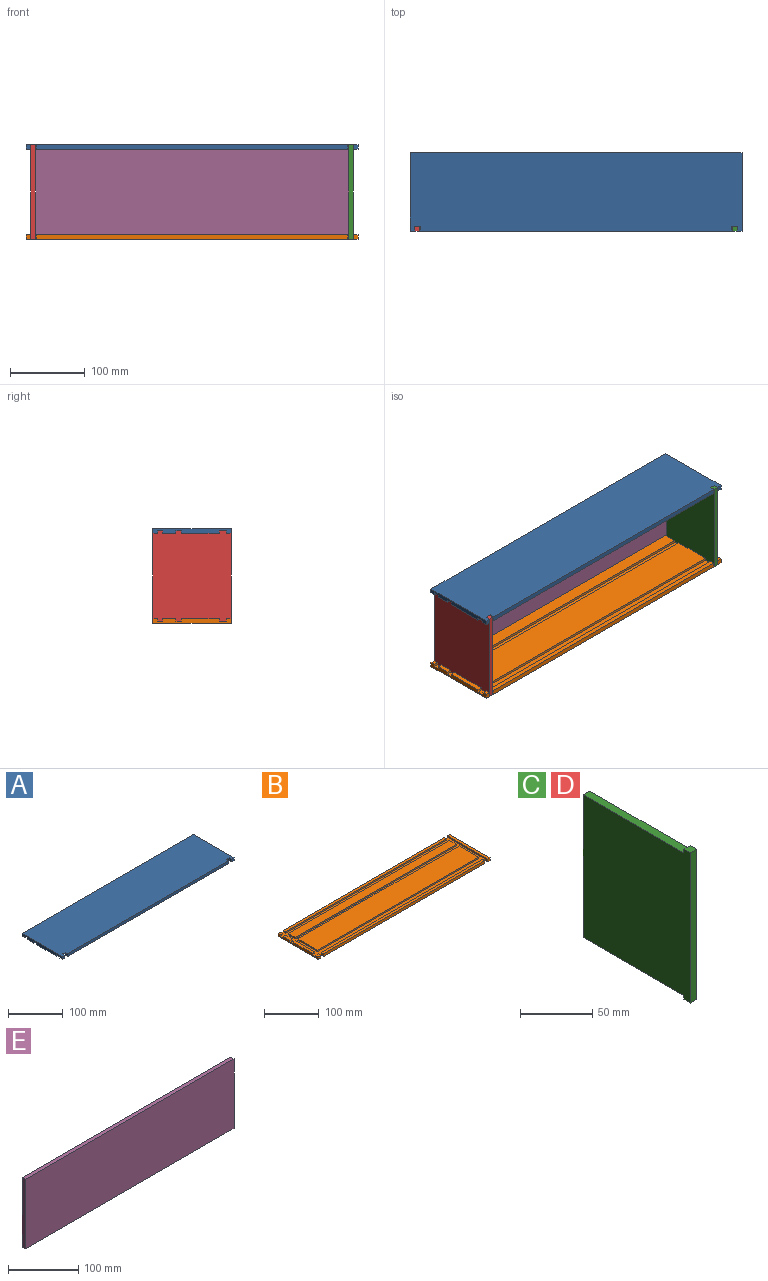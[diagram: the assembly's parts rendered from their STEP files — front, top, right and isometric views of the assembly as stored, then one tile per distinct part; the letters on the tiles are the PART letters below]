
ASSEMBLY  parts=5 mates=4
PART A: 44 faces, bbox 444.5x104.8x6.4 mm
  f0: plane 417.51x6.35mm, normal (0,0,-1), area 2651.2mm2, adj f12,f13,f14,f20
  f1: plane 6.35x6.35mm, normal (0,0,-1), area 40.3mm2, adj f8,f9,f10,f27
  f2: plane 50.8x6.35mm, normal (0,0,-1), area 322.6mm2, adj f8,f36,f37,f38
  f3: plane 17.46x6.35mm, normal (0,0,-1), area 110.9mm2, adj f8,f33,f34,f35
  f4: plane 417.51x6.35mm, normal (0,0,-1), area 2651.2mm2, adj f7,f28,f29,f30
  f5: plane 104.78x6.35mm, normal (0,0,-1), area 665.3mm2, adj f6,f7,f16,f17
  f6: plane 104.78x6.35mm, normal (1,0,0), area 665.3mm2, adj f5,f7,f17,f18
  f7: plane 444.5x6.35mm, normal (0,1,0), area 2777.2mm2, adj f4,f5,f6,f8,f16,f18,f19,f28
  f8: plane 104.78x6.35mm, normal (-1,0,0), area 589.7mm2, adj f1,f2,f3,f7,f9,f18,f19,f27
  f9: plane 6.35x6.35mm, normal (0,-1,0), area 40.3mm2, adj f1,f8,f10,f18
  f10: plane 6.35x6.35mm, normal (1,0,0), area 40.3mm2, adj f1,f9,f11,f18,f27
  f11: plane 7.14x3.18mm, normal (0,-1,0), area 22.7mm2, adj f10,f12,f18,f41
  f12: plane 6.35x6.35mm, normal (-1,0,0), area 40.3mm2, adj f0,f11,f13,f18,f20
  f13: plane 417.51x6.35mm, normal (0,-1,0), area 2651.2mm2, adj f0,f12,f14,f18
  f14: plane 6.35x6.35mm, normal (1,0,0), area 40.3mm2, adj f0,f13,f15,f18,f20
  f15: plane 7.14x3.18mm, normal (0,-1,0), area 22.7mm2, adj f14,f16,f18,f41
  f16: plane 104.78x6.35mm, normal (-1,0,0), area 352.8mm2, adj f5,f7,f15,f17,f18,f41
  f17: plane 6.35x6.35mm, normal (0,-1,0), area 40.3mm2, adj f5,f6,f16,f18
  f18: plane 444.5x104.78mm, normal (0,0,1), area 46481.8mm2, adj f6,f7,f8,f9,f10,f11,f12,f13
  f19: plane 6.35x6.35mm, normal (0,0,-1), area 40.3mm2, adj f7,f8,f31,f32
  f20: plane 417.51x3.18mm, normal (0,1,0), area 1325.6mm2, adj f0,f12,f14,f41
  f21: plane 417.51x3.18mm, normal (0,-1,0), area 1325.6mm2, adj f22,f40,f41,f43
  f22: plane 17.46x3.18mm, normal (-1,0,0), area 55.4mm2, adj f21,f23,f41,f43
  f23: plane 417.51x3.18mm, normal (0,1,0), area 1325.6mm2, adj f22,f40,f41,f43
  f24: plane 417.51x3.18mm, normal (0,-1,0), area 1325.6mm2, adj f25,f39,f41,f42
  f25: plane 50.8x3.18mm, normal (-1,0,0), area 161.3mm2, adj f24,f26,f41,f42
  f26: plane 417.51x3.18mm, normal (0,1,0), area 1325.6mm2, adj f25,f39,f41,f42
  f27: plane 6.35x3.18mm, normal (0,1,0), area 20.2mm2, adj f1,f8,f10,f41
  f28: plane 6.35x3.18mm, normal (1,0,0), area 20.2mm2, adj f4,f7,f29,f41
  f29: plane 417.51x3.18mm, normal (0,-1,0), area 1325.6mm2, adj f4,f28,f30,f41
  f30: plane 6.35x3.18mm, normal (-1,0,0), area 20.2mm2, adj f4,f7,f29,f41
  f31: plane 6.35x3.18mm, normal (1,0,0), area 20.2mm2, adj f7,f19,f32,f41
  f32: plane 6.35x3.18mm, normal (0,-1,0), area 20.2mm2, adj f8,f19,f31,f41
  f33: plane 6.35x3.18mm, normal (0,1,0), area 20.2mm2, adj f3,f8,f34,f41
  f34: plane 17.46x3.18mm, normal (1,0,0), area 55.4mm2, adj f3,f33,f35,f41
  f35: plane 6.35x3.18mm, normal (0,-1,0), area 20.2mm2, adj f3,f8,f34,f41
  f36: plane 6.35x3.18mm, normal (0,1,0), area 20.2mm2, adj f2,f8,f37,f41
  f37: plane 50.8x3.18mm, normal (1,0,0), area 161.3mm2, adj f2,f36,f38,f41
  f38: plane 6.35x3.18mm, normal (0,-1,0), area 20.2mm2, adj f2,f8,f37,f41
  f39: plane 50.8x3.18mm, normal (1,0,0), area 161.3mm2, adj f24,f26,f41,f42
  f40: plane 17.46x3.18mm, normal (1,0,0), area 55.4mm2, adj f21,f23,f41,f43
  f41: plane 438.15x98.43mm, normal (0,0,-1), area 11499.5mm2, adj f7,f8,f11,f15,f16,f20,f21,f22
  f42: plane 417.51x50.8mm, normal (0,0,-1), area 21209.6mm2, adj f24,f25,f26,f39
  f43: plane 417.51x17.46mm, normal (0,0,-1), area 7290.8mm2, adj f21,f22,f23,f40
PART B: 44 faces, bbox 444.5x104.8x6.4 mm
  f0: plane 444.5x6.35mm, normal (0,1,0), area 2777.2mm2, adj f1,f4,f5,f8,f9,f17,f19,f28
  f1: plane 104.78x6.35mm, normal (-1,0,0), area 589.7mm2, adj f0,f3,f6,f7,f8,f10,f19,f27
  f2: plane 417.51x6.35mm, normal (0,0,1), area 2651.2mm2, adj f13,f14,f15,f20
  f3: plane 6.35x6.35mm, normal (0,0,1), area 40.3mm2, adj f1,f10,f11,f27
  f4: plane 104.78x6.35mm, normal (0,0,1), area 665.3mm2, adj f0,f9,f17,f18
  f5: plane 417.51x6.35mm, normal (0,0,1), area 2651.2mm2, adj f0,f28,f29,f30
  f6: plane 17.46x6.35mm, normal (0,0,1), area 110.9mm2, adj f1,f33,f34,f35
  f7: plane 50.8x6.35mm, normal (0,0,1), area 322.6mm2, adj f1,f36,f37,f38
  f8: plane 6.35x6.35mm, normal (0,0,1), area 40.3mm2, adj f0,f1,f31,f32
  f9: plane 104.78x6.35mm, normal (1,0,0), area 665.3mm2, adj f0,f4,f18,f19
  f10: plane 6.35x6.35mm, normal (0,-1,0), area 40.3mm2, adj f1,f3,f11,f19
  f11: plane 6.35x6.35mm, normal (1,0,0), area 40.3mm2, adj f3,f10,f12,f19,f27
  f12: plane 7.14x3.18mm, normal (0,-1,0), area 22.7mm2, adj f11,f13,f19,f41
  f13: plane 6.35x6.35mm, normal (-1,0,0), area 40.3mm2, adj f2,f12,f14,f19,f20
  f14: plane 417.51x6.35mm, normal (0,-1,0), area 2651.2mm2, adj f2,f13,f15,f19
  f15: plane 6.35x6.35mm, normal (1,0,0), area 40.3mm2, adj f2,f14,f16,f19,f20
  f16: plane 7.14x3.18mm, normal (0,-1,0), area 22.7mm2, adj f15,f17,f19,f41
  f17: plane 104.78x6.35mm, normal (-1,0,0), area 352.8mm2, adj f0,f4,f16,f18,f19,f41
  f18: plane 6.35x6.35mm, normal (0,-1,0), area 40.3mm2, adj f4,f9,f17,f19
  f19: plane 444.5x104.78mm, normal (0,0,-1), area 46481.8mm2, adj f0,f1,f9,f10,f11,f12,f13,f14
  f20: plane 417.51x3.18mm, normal (0,1,0), area 1325.6mm2, adj f2,f13,f15,f41
  f21: plane 417.51x3.18mm, normal (0,-1,0), area 1325.6mm2, adj f22,f40,f41,f43
  f22: plane 17.46x3.18mm, normal (-1,0,0), area 55.4mm2, adj f21,f23,f41,f43
  f23: plane 417.51x3.18mm, normal (0,1,0), area 1325.6mm2, adj f22,f40,f41,f43
  f24: plane 417.51x3.18mm, normal (0,-1,0), area 1325.6mm2, adj f25,f39,f41,f42
  f25: plane 50.8x3.18mm, normal (-1,0,0), area 161.3mm2, adj f24,f26,f41,f42
  f26: plane 417.51x3.18mm, normal (0,1,0), area 1325.6mm2, adj f25,f39,f41,f42
  f27: plane 6.35x3.18mm, normal (0,1,0), area 20.2mm2, adj f1,f3,f11,f41
  f28: plane 6.35x3.18mm, normal (1,0,0), area 20.2mm2, adj f0,f5,f29,f41
  f29: plane 417.51x3.18mm, normal (0,-1,0), area 1325.6mm2, adj f5,f28,f30,f41
  f30: plane 6.35x3.18mm, normal (-1,0,0), area 20.2mm2, adj f0,f5,f29,f41
  f31: plane 6.35x3.18mm, normal (1,0,0), area 20.2mm2, adj f0,f8,f32,f41
  f32: plane 6.35x3.18mm, normal (0,-1,0), area 20.2mm2, adj f1,f8,f31,f41
  f33: plane 6.35x3.18mm, normal (0,1,0), area 20.2mm2, adj f1,f6,f34,f41
  f34: plane 17.46x3.18mm, normal (1,0,0), area 55.4mm2, adj f6,f33,f35,f41
  f35: plane 6.35x3.18mm, normal (0,-1,0), area 20.2mm2, adj f1,f6,f34,f41
  f36: plane 6.35x3.18mm, normal (0,1,0), area 20.2mm2, adj f1,f7,f37,f41
  f37: plane 50.8x3.18mm, normal (1,0,0), area 161.3mm2, adj f7,f36,f38,f41
  f38: plane 6.35x3.18mm, normal (0,-1,0), area 20.2mm2, adj f1,f7,f37,f41
  f39: plane 50.8x3.18mm, normal (1,0,0), area 161.3mm2, adj f24,f26,f41,f42
  f40: plane 17.46x3.18mm, normal (1,0,0), area 55.4mm2, adj f21,f23,f41,f43
  f41: plane 438.15x98.43mm, normal (0,0,1), area 11499.5mm2, adj f0,f1,f12,f16,f17,f20,f21,f22
  f42: plane 417.51x50.8mm, normal (0,0,1), area 21209.6mm2, adj f24,f25,f26,f39
  f43: plane 417.51x17.46mm, normal (0,0,1), area 7290.8mm2, adj f21,f22,f23,f40
PART C: 10 faces, bbox 6.4x104.8x127 mm
  f0: plane 98.43x6.35mm, normal (0,0,1), area 625mm2, adj f1,f7,f8,f9
  f1: plane 6.35x3.18mm, normal (0,1,0), area 20.2mm2, adj f0,f2,f8,f9
  f2: plane 6.35x6.35mm, normal (0,0,1), area 40.3mm2, adj f1,f3,f8,f9
  f3: plane 127x6.35mm, normal (0,-1,0), area 806.5mm2, adj f2,f4,f8,f9
  f4: plane 6.35x6.35mm, normal (0,0,-1), area 40.3mm2, adj f3,f5,f8,f9
  f5: plane 6.35x3.18mm, normal (0,1,0), area 20.2mm2, adj f4,f6,f8,f9
  f6: plane 98.43x6.35mm, normal (0,0,-1), area 625mm2, adj f5,f7,f8,f9
  f7: plane 120.65x6.35mm, normal (0,1,0), area 766.1mm2, adj f0,f6,f8,f9
  f8: plane 127x104.78mm, normal (1,0,0), area 12681.4mm2, adj f0,f1,f2,f3,f4,f5,f6,f7
  f9: plane 127x104.78mm, normal (-1,0,0), area 12681.4mm2, adj f0,f1,f2,f3,f4,f5,f6,f7
PART D: same geometry as C
PART E: 6 faces, bbox 419.1x6.4x120.7 mm
  f0: plane 419.1x6.35mm, normal (0,0,-1), area 2661.3mm2, adj f1,f3,f4,f5
  f1: plane 120.65x6.35mm, normal (1,0,0), area 766.1mm2, adj f0,f2,f4,f5
  f2: plane 419.1x6.35mm, normal (0,0,1), area 2661.3mm2, adj f1,f3,f4,f5
  f3: plane 120.65x6.35mm, normal (-1,0,0), area 766.1mm2, adj f0,f2,f4,f5
  f4: plane 419.1x120.65mm, normal (0,-1,0), area 50564.4mm2, adj f0,f1,f2,f3
  f5: plane 419.1x120.65mm, normal (0,1,0), area 50564.4mm2, adj f0,f1,f2,f3
PLACE A t=(289,53.78,-52.13)mm
PLACE B t=(289,53.78,-166.43)mm
PLACE C t=(498.55,53.78,-109.28)mm
PLACE D t=(73.1,53.78,-109.28)mm
PLACE E t=(289.42,99.38,-109.28)mm
MATE planar E.f0 <-> B.f41  axis (0,0,-1) through (289.42,96.2,-169.61)mm
MATE fastened C.f3 <-> B.f18  axis (0,-1,0) through (504.9,1.4,-172.78)mm
MATE fastened D.f3 <-> B.f10  axis (0,-1,0) through (73.1,1.4,-172.78)mm
MATE fastened A.f9 <-> D.f3  axis (0,-1,0) through (73.1,1.4,-45.78)mm
